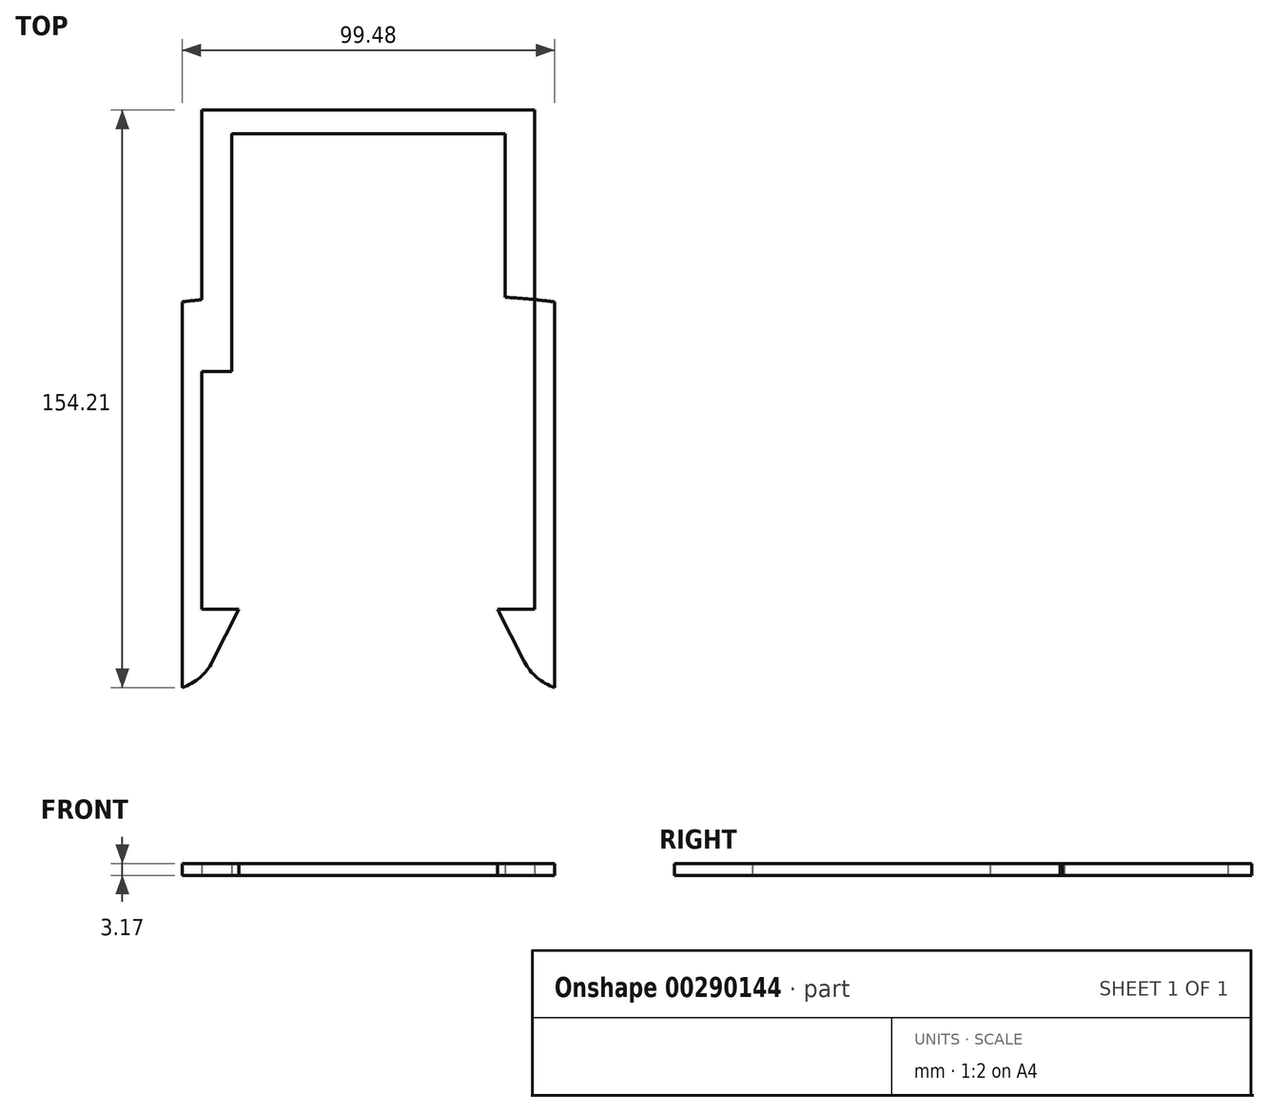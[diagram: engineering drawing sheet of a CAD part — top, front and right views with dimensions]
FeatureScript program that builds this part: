
annotation { "Feature Type Name" : "Feature", "Feature Type Description" : "" }
export const myFeature = defineFeature(function(context is Context, id is Id, definition is map)
    precondition{}
    {
        {
            var Q0;
            Q0=qCreatedBy(makeId("Top.planeOp"),FACE);
            var sketch = newSketch(context, id + "F0", { "sketchPlane" : qUnion([Q0])});
            skLineSegment(sketch, "E0", {"start": v(0, 58.2) * mm, "end": v(-27.09, 58.2) * mm});
            skLineSegment(sketch, "E1", {"start": v(0, -13.7) * mm, "end": v(-21.95, -13.7) * mm});
            skLineSegment(sketch, "E2", {"start": v(-31.65, -19.68) * mm, "end": v(-41.64, -39.37) * mm});
            skArc(sketch, "E3", {"start": v(-21.95, -13.7) * mm, "mid": v(-27.65, -15.32) * mm, "end": v(-31.65, -19.68) * mm});
            skArc(sketch, "E4", {"start": v(-59.94, -45.52) * mm, "mid": v(-49.53, -46.2) * mm, "end": v(-41.64, -39.37) * mm});
            skArc(sketch, "E5", {"start": v(-76.84, -17.66) * mm, "mid": v(-73.68, -34.8) * mm, "end": v(-59.94, -45.52) * mm});
            skArc(sketch, "E6", {"start": v(-58.6, 52.52) * mm, "mid": v(-71.25, 18.35) * mm, "end": v(-76.83, -17.66) * mm});
            skArc(sketch, "E7", {"start": v(-49.74, 56.7) * mm, "mid": v(-54.5, 55.3) * mm, "end": v(-58.6, 52.52) * mm});
            skArc(sketch, "E8", {"start": v(-27.09, 58.2) * mm, "mid": v(-38.44, 57.83) * mm, "end": v(-49.74, 56.7) * mm});
            skArc(sketch, "E9.MirrorCS", {"start": v(27.09, 58.2) * mm, "mid": v(38.44, 57.83) * mm, "end": v(49.74, 56.7) * mm});
            skArc(sketch, "E10.MirrorCS", {"start": v(49.74, 56.7) * mm, "mid": v(54.5, 55.3) * mm, "end": v(58.6, 52.52) * mm});
            skArc(sketch, "E11.MirrorCS", {"start": v(21.95, -13.7) * mm, "mid": v(27.65, -15.32) * mm, "end": v(31.65, -19.68) * mm});
            skLineSegment(sketch, "E12.MirrorCS", {"start": v(0, -13.7) * mm, "end": v(21.95, -13.7) * mm});
            skArc(sketch, "E13.MirrorCS", {"start": v(59.94, -45.52) * mm, "mid": v(49.53, -46.2) * mm, "end": v(41.64, -39.37) * mm});
            skArc(sketch, "E14.MirrorCS", {"start": v(76.84, -17.66) * mm, "mid": v(73.68, -34.8) * mm, "end": v(59.94, -45.52) * mm});
            skArc(sketch, "E15.MirrorCS", {"start": v(58.6, 52.52) * mm, "mid": v(71.25, 18.35) * mm, "end": v(76.83, -17.66) * mm});
            skLineSegment(sketch, "E16.MirrorCS", {"start": v(0, 58.2) * mm, "end": v(27.09, 58.2) * mm});
            skLineSegment(sketch, "E17.MirrorCS", {"start": v(31.65, -19.68) * mm, "end": v(41.64, -39.37) * mm});
            skLineSegment(sketch, "E18.bottom", {"start": v(-36.51, 101.6) * mm, "end": v(36.51, 101.6) * mm});
            skLineSegment(sketch, "E18.top", {"start": v(-36.51, 38.1) * mm, "end": v(36.51, 38.1) * mm});
            skLineSegment(sketch, "E18.left", {"start": v(-36.51, 101.6) * mm, "end": v(-36.51, 38.1) * mm});
            skLineSegment(sketch, "E18.right", {"start": v(36.51, 101.6) * mm, "end": v(36.51, 38.1) * mm});
            skPoint(sketch, "E18.middle", {"position": v(0, 69.85) * mm});
            skLineSegment(sketch, "E19.bottom", {"start": v(-44.45, -25.4) * mm, "end": v(44.45, -25.4) * mm});
            skLineSegment(sketch, "E19.top", {"start": v(-44.45, 38.1) * mm, "end": v(44.45, 38.1) * mm});
            skLineSegment(sketch, "E19.left", {"start": v(-44.45, -25.4) * mm, "end": v(-44.45, 38.1) * mm});
            skLineSegment(sketch, "E19.right", {"start": v(44.45, -25.4) * mm, "end": v(44.45, 38.1) * mm});
            skPoint(sketch, "E19.middle", {"position": v(0, 6.35) * mm});
            skLineSegment(sketch, "E20", {"start": v(-44.45, 38.1) * mm, "end": v(-44.45, 107.95) * mm});
            skLineSegment(sketch, "E21", {"start": v(-44.45, 107.95) * mm, "end": v(44.45, 107.95) * mm});
            skLineSegment(sketch, "E22", {"start": v(44.45, 107.95) * mm, "end": v(44.45, 38.1) * mm});
            skLineSegment(sketch, "E23", {"start": v(-49.74, 56.7) * mm, "end": v(-49.74, -46.26) * mm});
            skLineSegment(sketch, "E24", {"start": v(49.74, 56.7) * mm, "end": v(49.74, -46.26) * mm});
            skSolve(sketch);
        }
        {
            var Q0;
            {var subQ0=sQuery(id+"F0.wireOp",EDGE,"E20");var subQ1=sQuery(id+"F0.wireOp",EDGE,"E8");var subQ2=makeQuery(id+"F0.imprint","INTERSECT",VERTEX,{"derivedFrom":[subQ1,subQ0]});Q0=makeQuery(id+"F0.imprint","IMPRINT",FACE,{"disambiguationData":[TD([[makeQuery(id+"F0.imprint","IMPRINT",EDGE,{"disambiguationData":[TD([[subQ2,1.0]])],"derivedFrom":subQ1}),1.0]])]});}
            var Q1;
            {var subQ0=sQuery(id+"F0.wireOp",EDGE,"E18.bottom");Q1=makeQuery(id+"F0.imprint","IMPRINT",FACE,{"disambiguationData":[TD([[makeQuery(id+"F0.imprint","IMPRINT",EDGE,{"derivedFrom":subQ0}),1.0]])]});}
            var Q2;
            {var subQ0=sQuery(id+"F0.wireOp",EDGE,"E22");var subQ1=sQuery(id+"F0.wireOp",EDGE,"E9.MirrorCS");var subQ2=makeQuery(id+"F0.imprint","INTERSECT",VERTEX,{"derivedFrom":[subQ1,subQ0]});Q2=makeQuery(id+"F0.imprint","IMPRINT",FACE,{"disambiguationData":[TD([[makeQuery(id+"F0.imprint","IMPRINT",EDGE,{"disambiguationData":[TD([[subQ2,1.0]])],"derivedFrom":subQ1}),-1.0]])]});}
            var Q3;
            {var subQ0=sQuery(id+"F0.wireOp",EDGE,"E19.left");Q3=makeQuery(id+"F0.imprint","IMPRINT",FACE,{"disambiguationData":[TD([[makeQuery(id+"F0.imprint","IMPRINT",EDGE,{"derivedFrom":subQ0}),1.0]])]});}
            var Q4;
            {var subQ0=sQuery(id+"F0.wireOp",EDGE,"E19.right");Q4=makeQuery(id+"F0.imprint","IMPRINT",FACE,{"disambiguationData":[TD([[makeQuery(id+"F0.imprint","IMPRINT",EDGE,{"derivedFrom":subQ0}),-1.0]])]});}
            extrude(context, id + "F1", {"entities" : qUnion([Q0, Q1, Q2, Q3, Q4]), "depth" : 3.17 * mm});
        }
    });
